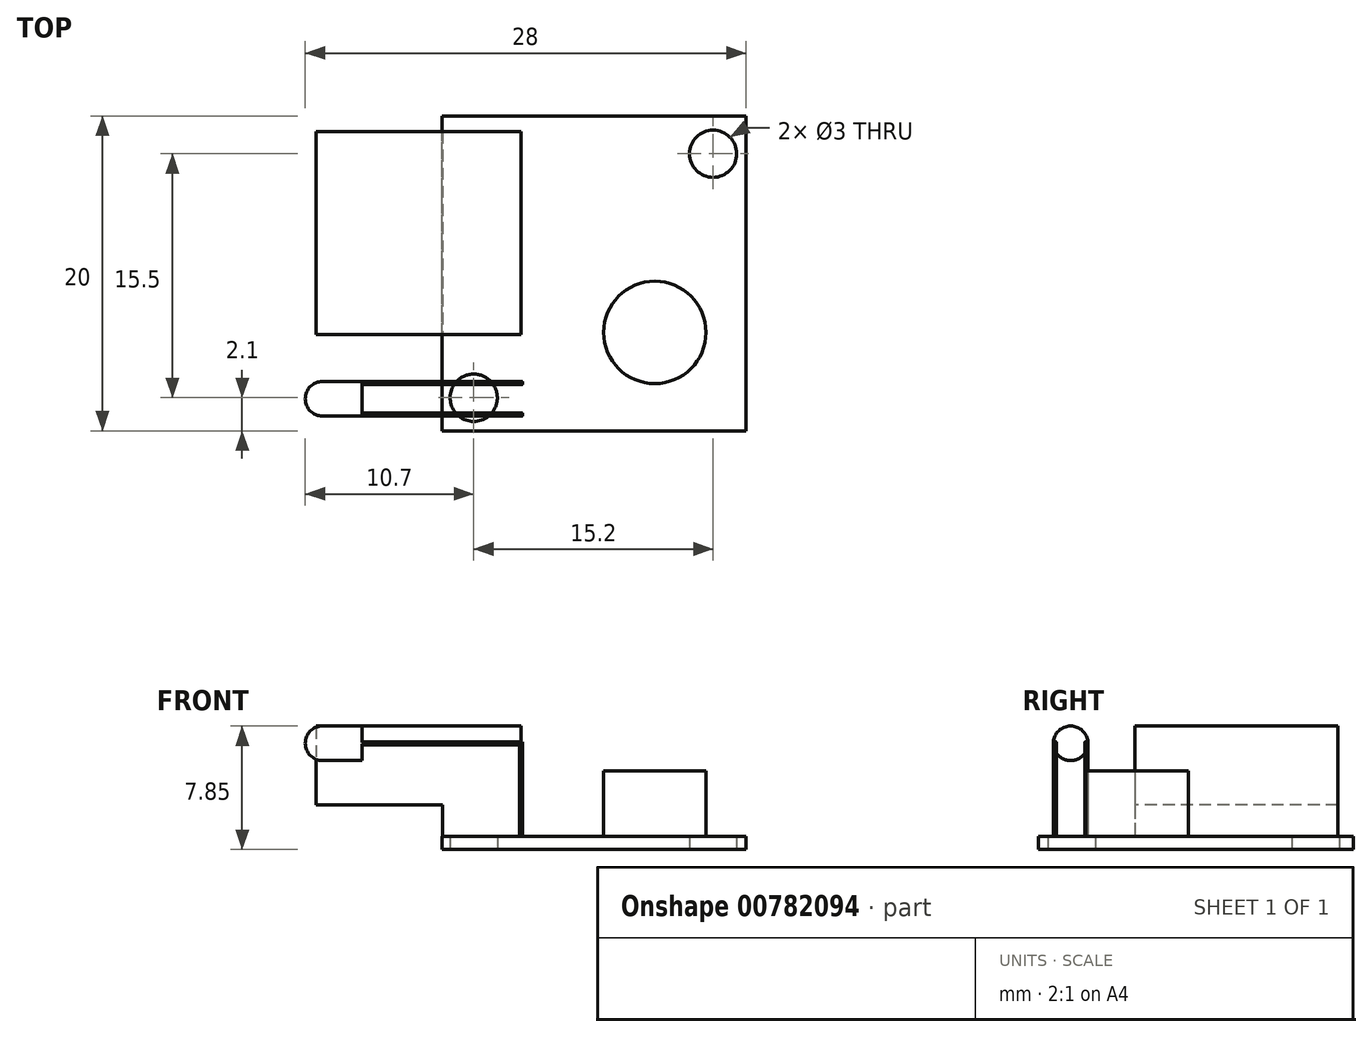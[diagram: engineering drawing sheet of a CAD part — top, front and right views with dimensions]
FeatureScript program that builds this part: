
annotation { "Feature Type Name" : "Feature", "Feature Type Description" : "" }
export const myFeature = defineFeature(function(context is Context, id is Id, definition is map)
    precondition{}
    {
        {
            var Q0;
            Q0=qCreatedBy(makeId("Top.planeOp"),FACE);
            var sketch = newSketch(context, id + "F0", { "sketchPlane" : qUnion([Q0])});
            skLineSegment(sketch, "E0.bottom", {"start": v(0, 0) * mm, "end": v(-19.3, 0) * mm});
            skLineSegment(sketch, "E0.top", {"start": v(0, 20) * mm, "end": v(-19.3, 20) * mm});
            skLineSegment(sketch, "E0.left", {"start": v(0, 0) * mm, "end": v(0, 20) * mm});
            skLineSegment(sketch, "E0.right", {"start": v(-19.3, 0) * mm, "end": v(-19.3, 20) * mm});
            skLineSegment(sketch, "E1", {"start": v(-18.65, 0) * mm, "end": v(-18.65, 0.6) * mm, "construction": true});
            skCircle(sketch, "E2", {"center": v(-17.3, 2.1) * mm, "radius": 1.5 * mm});
            skLineSegment(sketch, "E3", {"start": v(-17.3, 3.6) * mm, "end": v(-17.3, 0.6) * mm, "construction": true});
            skLineSegment(sketch, "E4", {"start": v(-18.8, 2.1) * mm, "end": v(-15.8, 2.1) * mm, "construction": true});
            skLineSegment(sketch, "E5", {"start": v(-19.3, 0.6) * mm, "end": v(-15.34, 0.6) * mm, "construction": true});
            skLineSegment(sketch, "E6", {"start": v(-19.3, 1.12) * mm, "end": v(-18.8, 1.12) * mm, "construction": true});
            skLineSegment(sketch, "E7", {"start": v(-18.8, 0) * mm, "end": v(-18.8, 3.12) * mm, "construction": true});
            skCircle(sketch, "E8", {"center": v(-2.1, 17.6) * mm, "radius": 1.5 * mm});
            skLineSegment(sketch, "E9", {"start": v(0, 18.55) * mm, "end": v(-0.6, 18.55) * mm, "construction": true});
            skLineSegment(sketch, "E10", {"start": v(-0.6, 20) * mm, "end": v(-0.6, 15.21) * mm, "construction": true});
            skLineSegment(sketch, "E11", {"start": v(-4.42, 20) * mm, "end": v(-4.42, 19.1) * mm});
            skLineSegment(sketch, "E12", {"start": v(-4.9, 19.1) * mm, "end": v(0.36, 19.1) * mm, "construction": true});
            skLineSegment(sketch, "E13", {"start": v(0, 4.09) * mm, "end": v(-2.55, 4.09) * mm, "construction": true});
            skLineSegment(sketch, "E14", {"start": v(-3.63, 0) * mm, "end": v(-3.63, 3) * mm, "construction": true});
            skLineSegment(sketch, "E15", {"start": v(-10.11, 3) * mm, "end": v(0, 3) * mm, "construction": true});
            skLineSegment(sketch, "E16", {"start": v(-2.55, 10.18) * mm, "end": v(-2.55, 0.4) * mm, "construction": true});
            skCircle(sketch, "E17", {"center": v(-5.8, 6.25) * mm, "radius": 3.25 * mm});
            skSolve(sketch);
        }
        {
            var Q0;
            Q0 = qSketchRegion(id + "F0", true);
            extrude(context, id + "F1", {"entities" : qUnion([Q0]), "depth" : 0.85 * mm, "offsetDistance" : 25 * mm});
        }
        {
            var Q0;
            Q0=makeQuery(id+"F1.opExtrude","CAP_FACE",FACE,{"disambiguationData":[OSD([sQuery(id+"F0.wireOp",EDGE,"E0.bottom"),sQuery(id+"F0.wireOp",EDGE,"E0.top"),sQuery(id+"F0.wireOp",EDGE,"E0.left"),sQuery(id+"F0.wireOp",EDGE,"E0.right")])],"isStart":false});
            var sketch = newSketch(context, id + "F2", { "sketchPlane" : qUnion([Q0])});
            skLineSegment(sketch, "E18", {"start": v(-19.3, 19) * mm, "end": v(-14.3, 19) * mm, "construction": true});
            skLineSegment(sketch, "E19", {"start": v(-14.3, 19) * mm, "end": v(-14.3, 20) * mm, "construction": true});
            skLineSegment(sketch, "E20.bottom", {"start": v(-14.3, 19) * mm, "end": v(-19.3, 19) * mm});
            skLineSegment(sketch, "E20.top", {"start": v(-14.3, 6.1) * mm, "end": v(-19.3, 6.1) * mm});
            skLineSegment(sketch, "E20.left", {"start": v(-14.3, 19) * mm, "end": v(-14.3, 6.1) * mm});
            skLineSegment(sketch, "E20.right", {"start": v(-19.3, 19) * mm, "end": v(-19.3, 6.1) * mm});
            skSolve(sketch);
        }
        {
            var Q0;
            Q0 = qSketchRegion(id + "F2", true);
            extrude(context, id + "F3", {"entities" : qUnion([Q0]), "operationType" : NewBodyOperationType.ADD, "depth" : 2 * mm, "offsetDistance" : 25 * mm});
        }
        {
            var Q0;
            Q0=makeQuery(id+"F3.opExtrude","CAP_FACE",FACE,{"disambiguationData":[OSD([sQuery(id+"F2.wireOp",EDGE,"E20.bottom"),sQuery(id+"F2.wireOp",EDGE,"E20.top"),sQuery(id+"F2.wireOp",EDGE,"E20.left"),sQuery(id+"F2.wireOp",EDGE,"E20.right")])],"isStart":false});
            var sketch = newSketch(context, id + "F4", { "sketchPlane" : qUnion([Q0])});
            skLineSegment(sketch, "E21.bottom", {"start": v(-14.3, 19) * mm, "end": v(-27.3, 19) * mm});
            skLineSegment(sketch, "E21.top", {"start": v(-14.3, 6.1) * mm, "end": v(-27.3, 6.1) * mm});
            skLineSegment(sketch, "E21.left", {"start": v(-14.3, 19) * mm, "end": v(-14.3, 6.1) * mm});
            skLineSegment(sketch, "E21.right", {"start": v(-27.3, 19) * mm, "end": v(-27.3, 6.1) * mm});
            skSolve(sketch);
        }
        {
            var Q0;
            Q0 = qSketchRegion(id + "F4", true);
            extrude(context, id + "F5", {"entities" : qUnion([Q0]), "operationType" : NewBodyOperationType.ADD, "depth" : 5 * mm, "offsetDistance" : 25 * mm});
        }
        {
            var Q0;
            Q0=makeQuery(id+"F0.imprint","IMPRINT",FACE,{"disambiguationData":[TD([[makeQuery(id+"F0.imprint","IMPRINT",EDGE,{"derivedFrom":sQuery(id+"F0.wireOp",EDGE,"E17")}),1.0]])]});
            extrude(context, id + "F6", {"entities" : qUnion([Q0]), "operationType" : NewBodyOperationType.ADD, "depth" : 5 * mm, "offsetDistance" : 25 * mm});
        }
        {
            var Q0;
            Q0=makeQuery(id+"F1.opExtrude","CAP_FACE",FACE,{"disambiguationData":[OSD([sQuery(id+"F0.wireOp",EDGE,"E0.bottom"),sQuery(id+"F0.wireOp",EDGE,"E0.top"),sQuery(id+"F0.wireOp",EDGE,"E0.left"),sQuery(id+"F0.wireOp",EDGE,"E0.right"),sQuery(id+"F0.wireOp",EDGE,"E2"),sQuery(id+"F0.wireOp",EDGE,"E8"),sQuery(id+"F0.wireOp",EDGE,"E17")])],"isStart":false});
            var sketch = newSketch(context, id + "F7", { "sketchPlane" : qUnion([Q0])});
            skLineSegment(sketch, "E22", {"start": v(-19.3, 0.48) * mm, "end": v(-14.3, 0.48) * mm, "construction": true});
            skLineSegment(sketch, "E23", {"start": v(-14.3, 0) * mm, "end": v(-14.3, 5.4) * mm, "construction": true});
            skLineSegment(sketch, "E24", {"start": v(-14.3, 0) * mm, "end": v(-14.3, 1.03) * mm, "construction": true});
            skLineSegment(sketch, "E25", {"start": v(-14.3, 1.03) * mm, "end": v(-14.3, 3.03) * mm, "construction": true});
            skLineSegment(sketch, "E26.bottom", {"start": v(-14.4, 3.13) * mm, "end": v(-14.2, 3.13) * mm});
            skLineSegment(sketch, "E26.top", {"start": v(-14.4, 2.93) * mm, "end": v(-14.2, 2.93) * mm});
            skLineSegment(sketch, "E26.left", {"start": v(-14.4, 3.13) * mm, "end": v(-14.4, 2.93) * mm});
            skLineSegment(sketch, "E26.right", {"start": v(-14.2, 3.13) * mm, "end": v(-14.2, 2.93) * mm});
            skPoint(sketch, "E26.middle", {"position": v(-14.3, 3.03) * mm});
            skLineSegment(sketch, "E27.bottom", {"start": v(-14.2, 1.13) * mm, "end": v(-14.4, 1.13) * mm});
            skLineSegment(sketch, "E27.top", {"start": v(-14.2, 0.93) * mm, "end": v(-14.4, 0.93) * mm});
            skLineSegment(sketch, "E27.left", {"start": v(-14.2, 1.13) * mm, "end": v(-14.2, 0.93) * mm});
            skLineSegment(sketch, "E27.right", {"start": v(-14.4, 1.13) * mm, "end": v(-14.4, 0.93) * mm});
            skPoint(sketch, "E27.middle", {"position": v(-14.3, 1.03) * mm});
            skSolve(sketch);
        }
        {
            var Q0;
            Q0 = qSketchRegion(id + "F7", true);
            extrude(context, id + "F8", {"entities" : qUnion([Q0]), "operationType" : NewBodyOperationType.ADD, "depth" : 6 * mm, "offsetDistance" : 25 * mm});
        }
        {
            var Q0;
            Q0=makeQuery(id+"F8.opExtrude","SWEPT_FACE",FACE,{"disambiguationData":[OSD([sQuery(id+"F7.wireOp",EDGE,"E26.left")])]});
            var sketch = newSketch(context, id + "F9", { "sketchPlane" : qUnion([Q0])});
            skLineSegment(sketch, "E28.bottom", {"start": v(-3.13, 6.85) * mm, "end": v(-2.93, 6.85) * mm});
            skLineSegment(sketch, "E28.top", {"start": v(-3.13, 6.65) * mm, "end": v(-2.93, 6.65) * mm});
            skLineSegment(sketch, "E28.left", {"start": v(-3.13, 6.85) * mm, "end": v(-3.13, 6.65) * mm});
            skLineSegment(sketch, "E28.right", {"start": v(-2.93, 6.85) * mm, "end": v(-2.93, 6.65) * mm});
            skLineSegment(sketch, "E29.bottom", {"start": v(-1.13, 6.85) * mm, "end": v(-0.93, 6.85) * mm});
            skLineSegment(sketch, "E29.top", {"start": v(-1.13, 6.65) * mm, "end": v(-0.93, 6.65) * mm});
            skLineSegment(sketch, "E29.left", {"start": v(-1.13, 6.85) * mm, "end": v(-1.13, 6.65) * mm});
            skLineSegment(sketch, "E29.right", {"start": v(-0.93, 6.85) * mm, "end": v(-0.93, 6.65) * mm});
            skSolve(sketch);
        }
        {
            var Q0;
            Q0 = qSketchRegion(id + "F9", true);
            extrude(context, id + "F10", {"entities" : qUnion([Q0]), "operationType" : NewBodyOperationType.ADD, "depth" : 10 * mm, "offsetDistance" : 25 * mm});
        }
        {
            var Q0;
            Q0=makeQuery(id+"F8.opExtrude","SWEPT_EDGE",EDGE,{"disambiguationData":[OSD([sQuery(id+"F7.wireOp",EDGE,"E26.top"),sQuery(id+"F7.wireOp",EDGE,"E26.left")])]});
            var Q1;
            Q1=makeQuery(id+"F8.opExtrude","SWEPT_EDGE",EDGE,{"disambiguationData":[OSD([sQuery(id+"F7.wireOp",EDGE,"E26.bottom"),sQuery(id+"F7.wireOp",EDGE,"E26.left")])]});
            var Q2;
            Q2=makeQuery(id+"F10.boolean.opBoolean","SPLIT",EDGE,{"derivedFrom":makeQuery(id+"F8.opExtrude","SWEPT_EDGE",EDGE,{"disambiguationData":[OSD([sQuery(id+"F7.wireOp",EDGE,"E27.bottom"),sQuery(id+"F7.wireOp",EDGE,"E27.right")])]})});
            var Q3;
            Q3=makeQuery(id+"F8.opExtrude","SWEPT_EDGE",EDGE,{"disambiguationData":[OSD([sQuery(id+"F7.wireOp",EDGE,"E27.top"),sQuery(id+"F7.wireOp",EDGE,"E27.left")])]});
            var Q4;
            Q4=makeQuery(id+"F8.opExtrude","SWEPT_EDGE",EDGE,{"disambiguationData":[OSD([sQuery(id+"F7.wireOp",EDGE,"E27.bottom"),sQuery(id+"F7.wireOp",EDGE,"E27.left")])]});
            var Q5;
            Q5=makeQuery(id+"F8.opExtrude","SWEPT_EDGE",EDGE,{"disambiguationData":[OSD([sQuery(id+"F7.wireOp",EDGE,"E26.top"),sQuery(id+"F7.wireOp",EDGE,"E26.right")])]});
            var Q6;
            Q6=makeQuery(id+"F8.opExtrude","SWEPT_EDGE",EDGE,{"disambiguationData":[OSD([sQuery(id+"F7.wireOp",EDGE,"E26.bottom"),sQuery(id+"F7.wireOp",EDGE,"E26.right")])]});
            var Q7;
            Q7=makeQuery(id+"F10.boolean.opBoolean","SPLIT",EDGE,{"derivedFrom":makeQuery(id+"F8.opExtrude","SWEPT_EDGE",EDGE,{"disambiguationData":[OSD([sQuery(id+"F7.wireOp",EDGE,"E27.top"),sQuery(id+"F7.wireOp",EDGE,"E27.right")])]})});
            var Q8;
            Q8=makeQuery(id+"F10.boolean.opBoolean","MERGE",EDGE,{"derivedFrom":[makeQuery(id+"F8.opExtrude","CAP_EDGE",EDGE,{"disambiguationData":[OSD([sQuery(id+"F7.wireOp",EDGE,"E27.top")])],"isStart":false}),makeQuery(id+"F10.opExtrude","SWEPT_EDGE",EDGE,{"disambiguationData":[OSD([sQuery(id+"F9.wireOp",EDGE,"E29.bottom"),sQuery(id+"F9.wireOp",EDGE,"E29.right")])]})]});
            var Q9;
            Q9=makeQuery(id+"F10.opExtrude","SWEPT_EDGE",EDGE,{"disambiguationData":[OSD([sQuery(id+"F9.wireOp",EDGE,"E29.top"),sQuery(id+"F9.wireOp",EDGE,"E29.right")])]});
            var Q10;
            Q10=makeQuery(id+"F10.boolean.opBoolean","MERGE",EDGE,{"derivedFrom":[makeQuery(id+"F8.opExtrude","CAP_EDGE",EDGE,{"disambiguationData":[OSD([sQuery(id+"F7.wireOp",EDGE,"E26.top")])],"isStart":false}),makeQuery(id+"F10.opExtrude","SWEPT_EDGE",EDGE,{"disambiguationData":[OSD([sQuery(id+"F9.wireOp",EDGE,"E28.bottom"),sQuery(id+"F9.wireOp",EDGE,"E28.right")])]})]});
            var Q11;
            Q11=makeQuery(id+"F10.opExtrude","SWEPT_EDGE",EDGE,{"disambiguationData":[OSD([sQuery(id+"F7.wireOp",EDGE,"E26.top"),sQuery(id+"F7.wireOp",EDGE,"E26.left"),sQuery(id+"F9.wireOp",EDGE,"E28.top"),sQuery(id+"F9.wireOp",EDGE,"E28.right")])]});
            var Q12;
            Q12=makeQuery(id+"F10.boolean.opBoolean","MERGE",EDGE,{"derivedFrom":[makeQuery(id+"F8.opExtrude","CAP_EDGE",EDGE,{"disambiguationData":[OSD([sQuery(id+"F7.wireOp",EDGE,"E27.bottom")])],"isStart":false}),makeQuery(id+"F10.opExtrude","SWEPT_EDGE",EDGE,{"disambiguationData":[OSD([sQuery(id+"F9.wireOp",EDGE,"E29.bottom"),sQuery(id+"F9.wireOp",EDGE,"E29.left")])]})]});
            var Q13;
            Q13=makeQuery(id+"F10.boolean.opBoolean","MERGE",EDGE,{"derivedFrom":[makeQuery(id+"F8.opExtrude","CAP_EDGE",EDGE,{"disambiguationData":[OSD([sQuery(id+"F7.wireOp",EDGE,"E26.bottom")])],"isStart":false}),makeQuery(id+"F10.opExtrude","SWEPT_EDGE",EDGE,{"disambiguationData":[OSD([sQuery(id+"F9.wireOp",EDGE,"E28.bottom"),sQuery(id+"F9.wireOp",EDGE,"E28.left")])]})]});
            var Q14;
            Q14=makeQuery(id+"F10.opExtrude","SWEPT_EDGE",EDGE,{"disambiguationData":[OSD([sQuery(id+"F9.wireOp",EDGE,"E29.top"),sQuery(id+"F9.wireOp",EDGE,"E29.left")])]});
            var Q15;
            Q15=makeQuery(id+"F10.opExtrude","SWEPT_EDGE",EDGE,{"disambiguationData":[OSD([sQuery(id+"F7.wireOp",EDGE,"E26.bottom"),sQuery(id+"F7.wireOp",EDGE,"E26.left"),sQuery(id+"F9.wireOp",EDGE,"E28.top"),sQuery(id+"F9.wireOp",EDGE,"E28.left")])]});
            fillet(context, id + "F11", {"entities" : qUnion([Q0, Q1, Q2, Q3, Q4, Q5, Q6, Q7, Q8, Q9, Q10, Q11, Q12, Q13, Q14, Q15]), "tangentPropagation" : true, "radius" : 0.05 * mm, "defaultsChanged" : false, "vertexSettings" : [], "allowEdgeOverflow" : false});
        }
        {
            var Q0;
            Q0=makeQuery(id+"F10.opExtrude","CAP_FACE",FACE,{"disambiguationData":[OSD([sQuery(id+"F9.wireOp",EDGE,"E28.bottom"),sQuery(id+"F9.wireOp",EDGE,"E28.top"),sQuery(id+"F9.wireOp",EDGE,"E28.left"),sQuery(id+"F9.wireOp",EDGE,"E28.right")])],"isStart":false});
            var sketch = newSketch(context, id + "F12", { "sketchPlane" : qUnion([Q0])});
            skCircle(sketch, "E30", {"center": v(-2.03, 6.75) * mm, "radius": 1.1 * mm});
            skSolve(sketch);
        }
        {
            var Q0;
            Q0 = qSketchRegion(id + "F12", true);
            extrude(context, id + "F13", {"entities" : qUnion([Q0]), "operationType" : NewBodyOperationType.ADD, "depth" : 2.5 * mm, "offsetDistance" : 25 * mm});
        }
        {
            var Q0;
            Q0=makeQuery(id+"F13.opExtrude","CAP_FACE",FACE,{"disambiguationData":[OSD([sQuery(id+"F12.wireOp",EDGE,"E30")])],"isStart":false});
            var sketch = newSketch(context, id + "F14", { "sketchPlane" : qUnion([Q0])});
            skLineSegment(sketch, "E31", {"start": v(-2.03, 6.75) * mm, "end": v(-2.03, 7.85) * mm});
            skLineSegment(sketch, "E32", {"start": v(-2.03, 6.75) * mm, "end": v(-2.03, 5.65) * mm});
            skArc(sketch, "E33", {"start": v(-2.03, 7.85) * mm, "mid": v(-3.13, 6.75) * mm, "end": v(-2.03, 5.65) * mm});
            skSolve(sketch);
        }
        {
            var Q0;
            Q0=makeQuery(id+"F14.imprint","IMPRINT",FACE,{"disambiguationData":[TD([[makeQuery(id+"F14.imprint","IMPRINT",EDGE,{"derivedFrom":sQuery(id+"F14.wireOp",EDGE,"E31")}),1.0]])]});
            var Q1;
            Q1=sQuery(id+"F14.wireOp",EDGE,"E31");
            revolve(context, id + "F15", {"operationType" : NewBodyOperationType.ADD, "surfaceOperationType" : NewSurfaceOperationType.NEW, "entities" : qUnion([Q0]), "axis" : qUnion([Q1]), "revolveType" : RevolveType.FULL});
        }
    });
